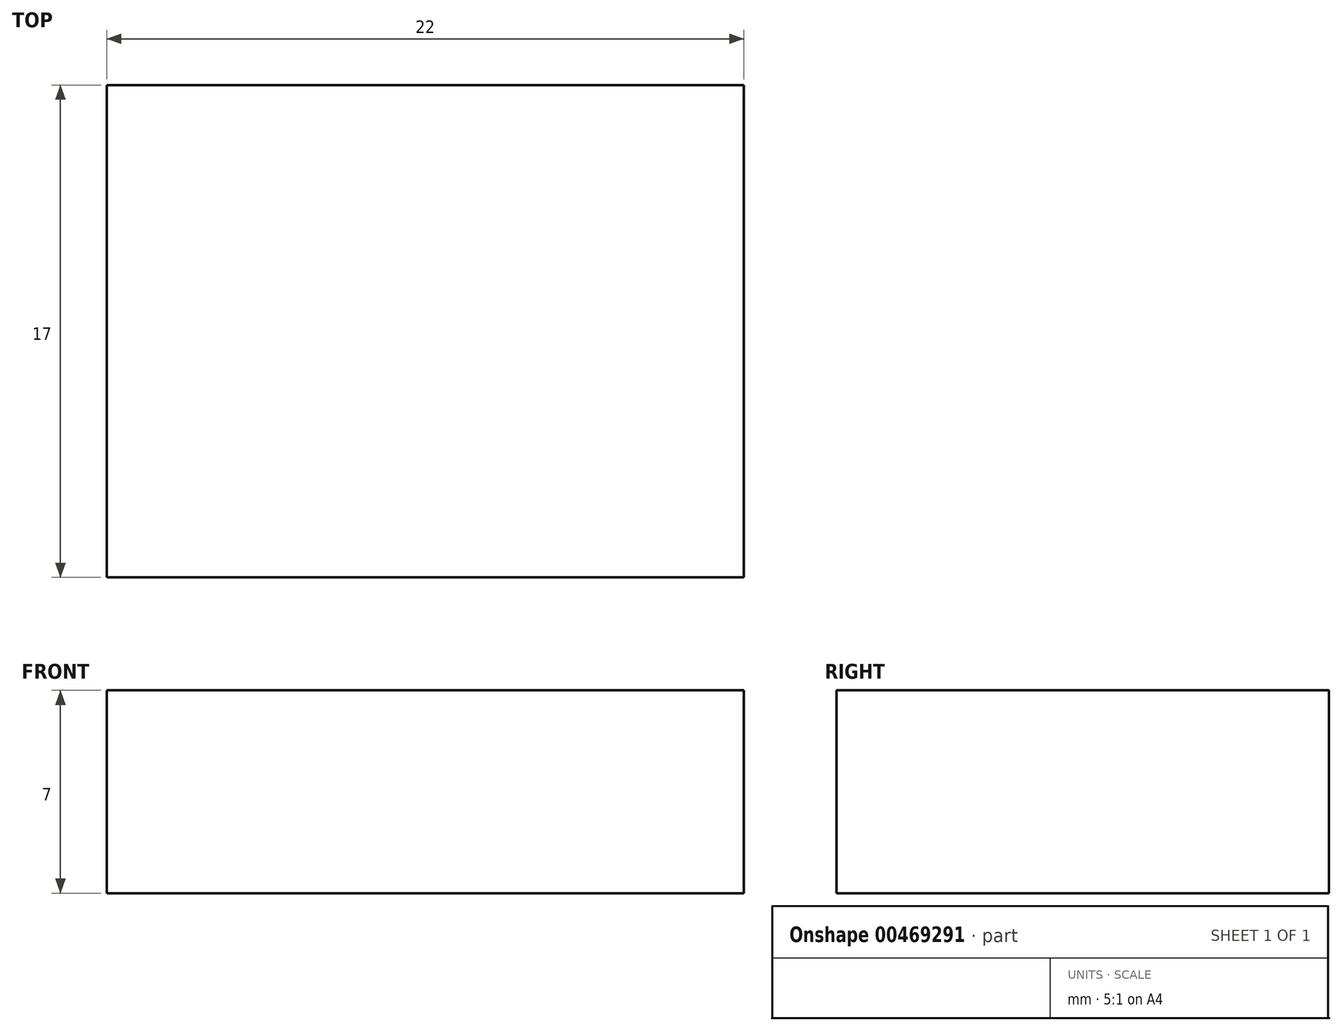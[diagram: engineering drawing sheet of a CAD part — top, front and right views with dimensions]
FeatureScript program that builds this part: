
annotation { "Feature Type Name" : "Feature", "Feature Type Description" : "" }
export const myFeature = defineFeature(function(context is Context, id is Id, definition is map)
    precondition{}
    {
        {
            var Q0;
            Q0=qCreatedBy(makeId("Top.planeOp"),FACE);
            var sketch = newSketch(context, id + "F0", { "sketchPlane" : qUnion([Q0])});
            skLineSegment(sketch, "E0.bottom", {"start": v(-11, 8.5) * mm, "end": v(11, 8.5) * mm});
            skLineSegment(sketch, "E0.top", {"start": v(-11, -8.5) * mm, "end": v(11, -8.5) * mm});
            skLineSegment(sketch, "E0.left", {"start": v(-11, 8.5) * mm, "end": v(-11, -8.5) * mm});
            skLineSegment(sketch, "E0.right", {"start": v(11, 8.5) * mm, "end": v(11, -8.5) * mm});
            skPoint(sketch, "E0.middle", {"position": v(0, 0) * mm});
            skSolve(sketch);
        }
        {
            var Q0;
            Q0 = qSketchRegion(id + "F0", true);
            extrude(context, id + "F1", {"entities" : qUnion([Q0]), "depth" : 7 * mm, "offsetDistance" : 25 * mm});
        }
    });
